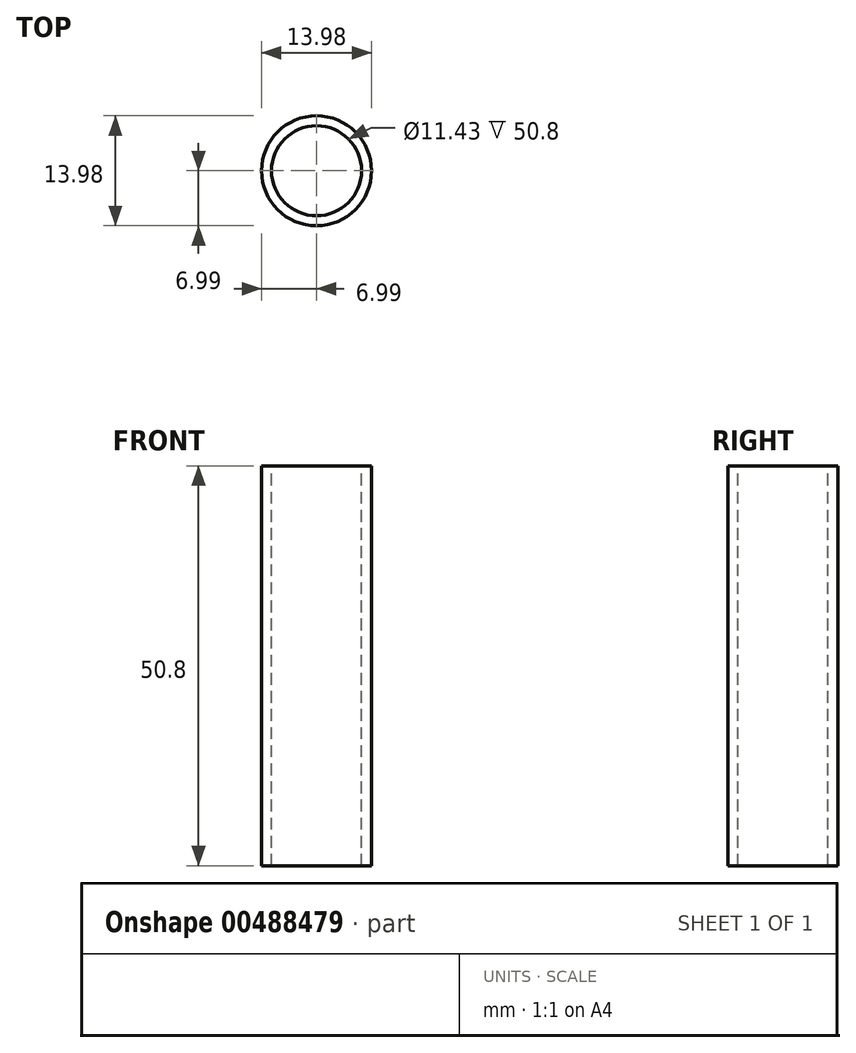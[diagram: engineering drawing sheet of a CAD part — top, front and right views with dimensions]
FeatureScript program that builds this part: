
annotation { "Feature Type Name" : "Feature", "Feature Type Description" : "" }
export const myFeature = defineFeature(function(context is Context, id is Id, definition is map)
    precondition{}
    {
        {
            var Q0;
            Q0=qCreatedBy(makeId("Top.planeOp"),FACE);
            var sketch = newSketch(context, id + "F0", { "sketchPlane" : qUnion([Q0])});
            skCircle(sketch, "E0", {"center": v(0, 0) * mm, "radius": 6.99 * mm});
            skCircle(sketch, "E1", {"center": v(0, 0) * mm, "radius": 5.72 * mm});
            skSolve(sketch);
        }
        {
            var Q0;
            Q0=makeQuery(id+"F0.imprint","IMPRINT",FACE,{"disambiguationData":[TD([[makeQuery(id+"F0.imprint","IMPRINT",EDGE,{"derivedFrom":sQuery(id+"F0.wireOp",EDGE,"E0")}),1.0]])]});
            extrude(context, id + "F1", {"entities" : qUnion([Q0]), "oppositeDirection" : true, "depth" : 50.8 * mm});
        }
    });
